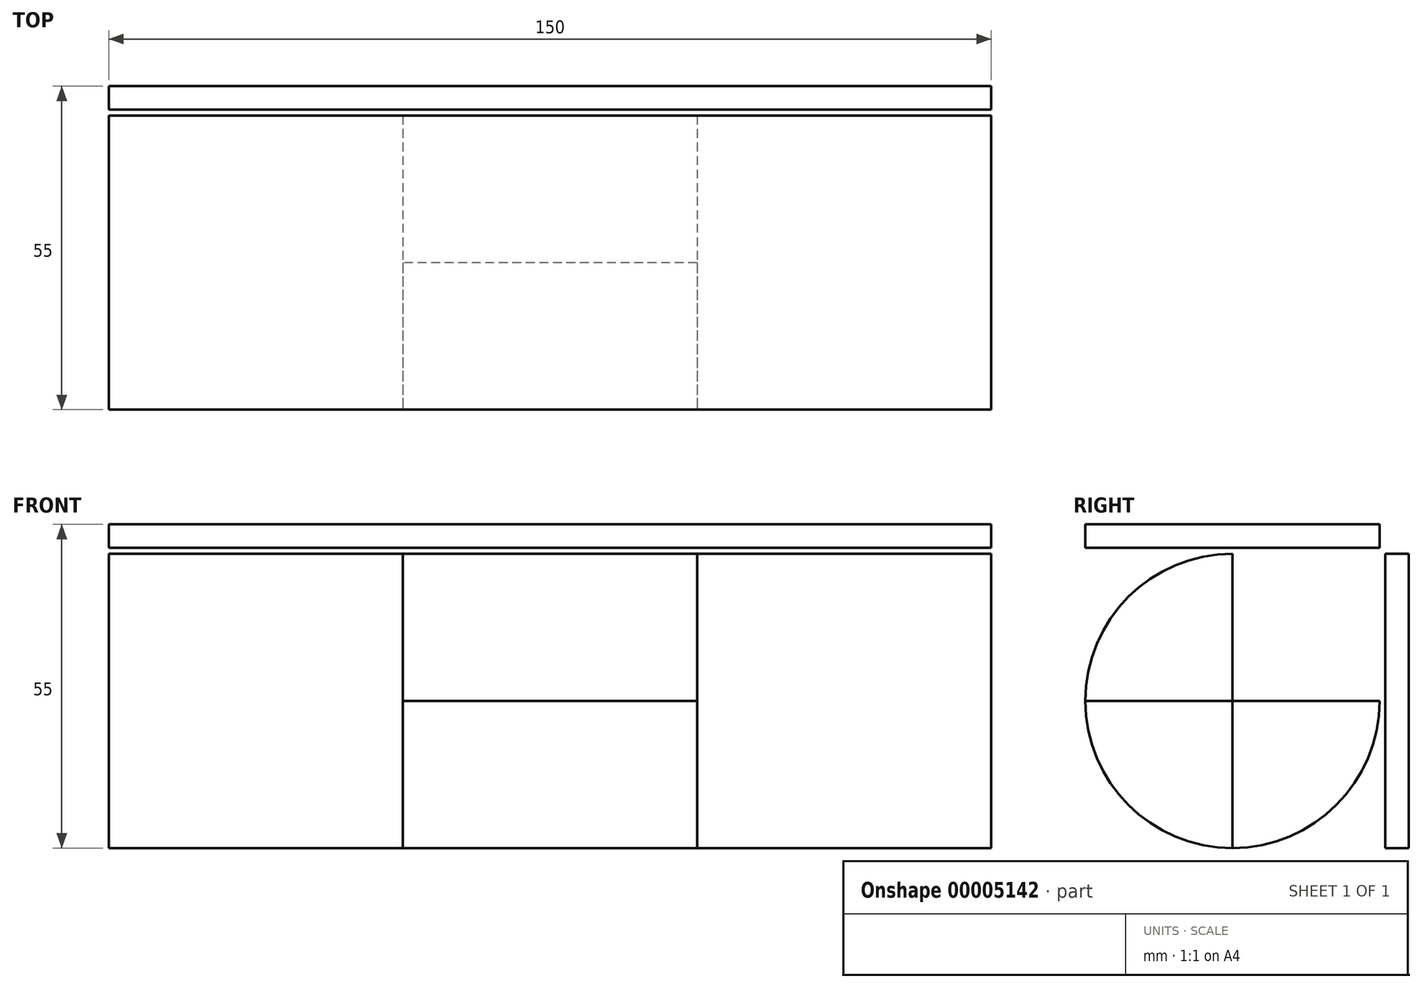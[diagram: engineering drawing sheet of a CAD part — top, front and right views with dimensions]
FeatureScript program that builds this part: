
annotation { "Feature Type Name" : "Feature", "Feature Type Description" : "" }
export const myFeature = defineFeature(function(context is Context, id is Id, definition is map)
    precondition{}
    {
        {
            var Q0;
            Q0=qCreatedBy(makeId("Right.planeOp"),FACE);
            var sketch = newSketch(context, id + "F0", { "sketchPlane" : qUnion([Q0])});
            skLineSegment(sketch, "E0.rect.bottom", {"start": v(-27.5, 25) * mm, "end": v(27.5, 25) * mm});
            skLineSegment(sketch, "E0.rect.top", {"start": v(-27.5, -25) * mm, "end": v(27.5, -25) * mm});
            skLineSegment(sketch, "E0.rect.left", {"start": v(-27.5, 25) * mm, "end": v(-27.5, -25) * mm});
            skLineSegment(sketch, "E0.rect.right", {"start": v(27.5, 25) * mm, "end": v(27.5, -25) * mm});
            skPoint(sketch, "E0.rect.middle", {"position": v(0, 0) * mm});
            skSolve(sketch);
        }
        {
            var Q0;
            Q0=makeQuery(id+"F0.imprint","IMPRINT",FACE,{"disambiguationData":[TD([[makeQuery(id+"F0.imprint","IMPRINT",EDGE,{"derivedFrom":sQuery(id+"F0.wireOp",EDGE,"E0.rect.bottom")}),-1.0]])]});
            extrude(context, id + "F1", {"entities" : qUnion([Q0]), "depth" : 150 * mm});
        }
        {
            var Q0;
            Q0=makeQuery(id+"F1.opExtrude","SWEPT_EDGE",EDGE,{"disambiguationData":[OSD([sQuery(id+"F0.wireOp",EDGE,"E0.rect.bottom"),sQuery(id+"F0.wireOp",EDGE,"E0.rect.left")])]});
            var Q1;
            Q1=makeQuery(id+"F1.opExtrude","SWEPT_EDGE",EDGE,{"disambiguationData":[OSD([sQuery(id+"F0.wireOp",EDGE,"E0.rect.top"),sQuery(id+"F0.wireOp",EDGE,"E0.rect.left")])]});
            fillet(context, id + "F2", {"entities" : qUnion([Q0, Q1]), "radius" : 25 * mm, "tangentPropagation" : true, "allowEdgeOverflow" : false});
        }
        {
            var Q0;
            Q0=makeQuery(id+"F1.opExtrude","SWEPT_BODY",BODY,{"disambiguationData":[OSD([sQuery(id+"F0.wireOp",EDGE,"E0.rect.bottom"),sQuery(id+"F0.wireOp",EDGE,"E0.rect.top"),sQuery(id+"F0.wireOp",EDGE,"E0.rect.left"),sQuery(id+"F0.wireOp",EDGE,"E0.rect.right")])]});
            var Q1;
            {var subQ0=sQuery(id+"F0.wireOp",EDGE,"E0.rect.top");var subQ1=sQuery(id+"F0.wireOp",EDGE,"E0.rect.left");Q1=makeQuery(id+"F2.opFillet","BLEND_EDGE",EDGE,{"blendedFrom":[makeQuery(id+"F1.opExtrude","SWEPT_EDGE",EDGE,{"disambiguationData":[OSD([subQ0,subQ1])]}),makeQuery(id+"F1.opExtrude","CAP_FACE",FACE,{"disambiguationData":[OSD([sQuery(id+"F0.wireOp",EDGE,"E0.rect.bottom"),subQ0,subQ1,sQuery(id+"F0.wireOp",EDGE,"E0.rect.right")])],"isStart":false})],"blendedInto":[makeQuery(id+"F1.opExtrude","CAP_FACE",FACE,{"disambiguationData":[OSD([sQuery(id+"F0.wireOp",EDGE,"E0.rect.bottom"),subQ0,subQ1,sQuery(id+"F0.wireOp",EDGE,"E0.rect.right")])],"isStart":false})]});}
            var Q2;
            Q2=makeQuery(id+"F1.opExtrude","CAP_EDGE",EDGE,{"disambiguationData":[OSD([sQuery(id+"F0.wireOp",EDGE,"E0.rect.bottom")])],"isStart":false});
            transform(context, id + "F3", {"entities" : qUnion([Q0]), "transformType" : TransformType.COPY});
        }
        {
            var Q0;
            Q0=makeQuery(id+"F1.opExtrude","SWEPT_FACE",FACE,{"disambiguationData":[OSD([sQuery(id+"F0.wireOp",EDGE,"E0.rect.bottom")])]});
            var sketch = newSketch(context, id + "F4", { "sketchPlane" : qUnion([Q0])});
            skLineSegment(sketch, "E1.0", {"start": v(0, -2.5) * mm, "end": v(0, -27.5) * mm, "construction": true});
            skLineSegment(sketch, "E1.1", {"start": v(150, -2.5) * mm, "end": v(150, -27.5) * mm, "construction": true});
            skLineSegment(sketch, "E2.bottom", {"start": v(0, 23.5) * mm, "end": v(150, 23.5) * mm});
            skLineSegment(sketch, "E2.top", {"start": v(0, -27.5) * mm, "end": v(150, -27.5) * mm});
            skLineSegment(sketch, "E2.left", {"start": v(0, 23.5) * mm, "end": v(0, -27.5) * mm});
            skLineSegment(sketch, "E2.right", {"start": v(150, 23.5) * mm, "end": v(150, -27.5) * mm});
            skLineSegment(sketch, "E3.bottom", {"start": v(50, 27.5) * mm, "end": v(100, 27.5) * mm});
            skLineSegment(sketch, "E3.top", {"start": v(50, -27.5) * mm, "end": v(100, -27.5) * mm});
            skLineSegment(sketch, "E3.left", {"start": v(50, 27.5) * mm, "end": v(50, -27.5) * mm});
            skLineSegment(sketch, "E3.right", {"start": v(100, 27.5) * mm, "end": v(100, -27.5) * mm});
            skLineSegment(sketch, "E4", {"start": v(75, 27.5) * mm, "end": v(75, -27.5) * mm, "construction": true});
            skSolve(sketch);
        }
        {
            var Q0;
            {var subQ7=sQuery(id+"F4.wireOp",EDGE,"E3.top");Q0=makeQuery(id+"F4.imprint","IMPRINT",FACE,{"disambiguationData":[TD([[makeQuery(id+"F4.imprint","IMPRINT",EDGE,{"derivedFrom":subQ7}),1.0]])]});}
            var Q1;
            {var subQ4=sQuery(id+"F4.wireOp",EDGE,"E3.left");var subQ6=sQuery(id+"F4.wireOp",EDGE,"E2.bottom");var subQ8=makeQuery(id+"F4.imprint","INTERSECT",VERTEX,{"derivedFrom":[subQ6,subQ4]});Q1=makeQuery(id+"F4.imprint","IMPRINT",FACE,{"disambiguationData":[TD([[makeQuery(id+"F4.imprint","IMPRINT",EDGE,{"disambiguationData":[TD([[subQ8,-1.0]])],"derivedFrom":subQ6}),-1.0]])]});}
            extrude(context, id + "F5", {"entities" : qUnion([Q0, Q1]), "operationType" : NewBodyOperationType.REMOVE, "endBound" : BoundingType.THROUGH_ALL, "oppositeDirection" : true, "depth" : 25 * mm});
        }
        {
            var Q0;
            {var subQ2=sQuery(id+"F4.wireOp",EDGE,"E3.left");var subQ6=sQuery(id+"F4.wireOp",EDGE,"E2.bottom");var subQ7=makeQuery(id+"F4.imprint","INTERSECT",VERTEX,{"derivedFrom":[subQ6,subQ2]});Q0=makeQuery(id+"F4.imprint","IMPRINT",FACE,{"disambiguationData":[TD([[makeQuery(id+"F4.imprint","IMPRINT",EDGE,{"disambiguationData":[TD([[subQ7,1.0]])],"derivedFrom":subQ6}),-1.0]])]});}
            var Q1;
            {var subQ4=sQuery(id+"F4.wireOp",EDGE,"E2.left");var subQ6=sQuery(id+"F4.wireOp",EDGE,"E2.top");var subQ8=makeQuery(id+"F4.imprint","INTERSECT",VERTEX,{"derivedFrom":[subQ6,subQ4]});Q1=makeQuery(id+"F4.imprint","IMPRINT",FACE,{"disambiguationData":[TD([[makeQuery(id+"F4.imprint","IMPRINT",EDGE,{"disambiguationData":[TD([[subQ8,-1.0]])],"derivedFrom":subQ6}),1.0]])]});}
            var Q2;
            {var subQ2=sQuery(id+"F4.wireOp",EDGE,"E3.right");var subQ6=sQuery(id+"F4.wireOp",EDGE,"E2.bottom");var subQ7=makeQuery(id+"F4.imprint","INTERSECT",VERTEX,{"derivedFrom":[subQ6,subQ2]});Q2=makeQuery(id+"F4.imprint","IMPRINT",FACE,{"disambiguationData":[TD([[makeQuery(id+"F4.imprint","IMPRINT",EDGE,{"disambiguationData":[TD([[subQ7,-1.0]])],"derivedFrom":subQ6}),-1.0]])]});}
            var Q3;
            {var subQ4=sQuery(id+"F4.wireOp",EDGE,"E2.right");var subQ6=sQuery(id+"F4.wireOp",EDGE,"E2.top");var subQ8=makeQuery(id+"F4.imprint","INTERSECT",VERTEX,{"derivedFrom":[subQ6,subQ4]});Q3=makeQuery(id+"F4.imprint","IMPRINT",FACE,{"disambiguationData":[TD([[makeQuery(id+"F4.imprint","IMPRINT",EDGE,{"disambiguationData":[TD([[subQ8,1.0]])],"derivedFrom":subQ6}),1.0]])]});}
            extrude(context, id + "F6", {"entities" : qUnion([Q0, Q1, Q2, Q3]), "operationType" : NewBodyOperationType.REMOVE, "endBound" : BoundingType.THROUGH_ALL, "oppositeDirection" : true, "depth" : 25 * mm});
        }
        {
            var Q0;
            Q0=makeQuery(id+"F1.opExtrude","SWEPT_BODY",BODY,{"disambiguationData":[OSD([sQuery(id+"F0.wireOp",EDGE,"E0.rect.bottom"),sQuery(id+"F0.wireOp",EDGE,"E0.rect.top"),sQuery(id+"F0.wireOp",EDGE,"E0.rect.left"),sQuery(id+"F0.wireOp",EDGE,"E0.rect.right")])]});
            var Q1;
            {var subQ0=sQuery(id+"F0.wireOp",EDGE,"E0.rect.top");var subQ1=sQuery(id+"F0.wireOp",EDGE,"E0.rect.left");Q1=makeQuery(id+"F5.boolean.opBoolean","SPLIT",FACE,{"disambiguationData":[TD([makeQuery(id+"F5.opExtrude","SWEPT_FACE",FACE,{"disambiguationData":[OSD([sQuery(id+"F4.wireOp",EDGE,"E3.right")])]})])],"derivedFrom":makeQuery(id+"F2.opFillet","BLEND_FACE",FACE,{"disambiguationData":[OSD([subQ0,subQ1])]})});}
            transform(context, id + "F7", {"entities" : qUnion([Q0]), "transformType" : TransformType.ROTATION, "transformAxis" : qUnion([Q1]), "angle" : 90 * degree, "makeCopy" : false});
        }
    });
